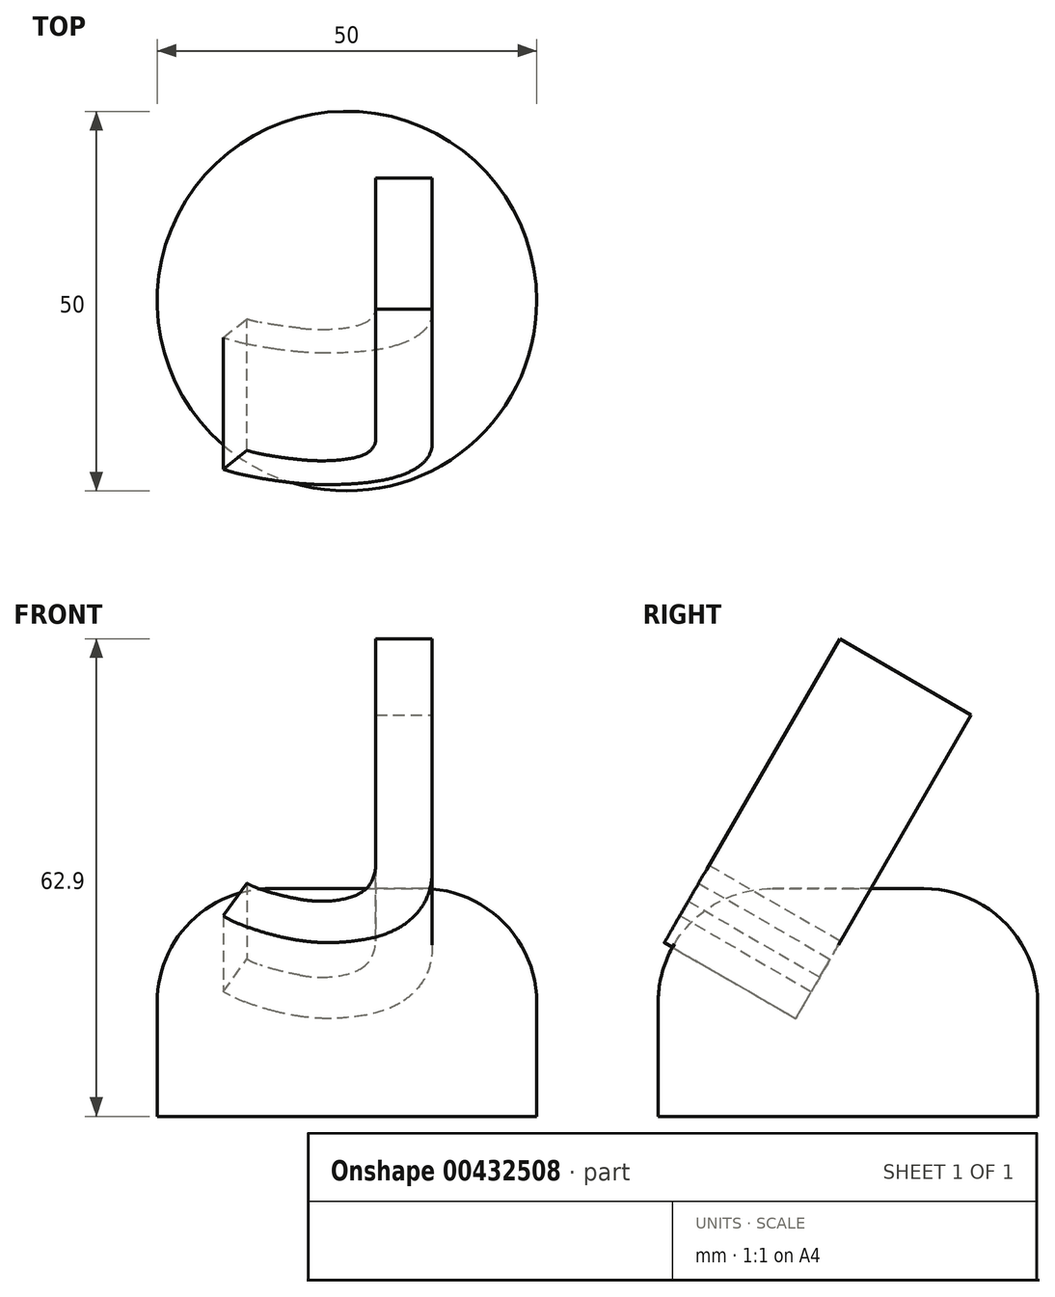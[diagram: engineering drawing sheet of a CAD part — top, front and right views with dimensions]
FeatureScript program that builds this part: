
annotation { "Feature Type Name" : "Feature", "Feature Type Description" : "" }
export const myFeature = defineFeature(function(context is Context, id is Id, definition is map)
    precondition{}
    {
        {
            var Q0;
            Q0=qCreatedBy(makeId("Top.planeOp"),FACE);
            var sketch = newSketch(context, id + "F0", { "sketchPlane" : qUnion([Q0])});
            skText(sketch, "E0", { "text": "J", "fontName": "AllertaStencil-Regular.ttf"});
            const initialGuessF0  = {"E0": [-0.05232, -0.03537, 1, 0, 0.045]};
            skSetInitialGuess(sketch, initialGuessF0);
            skSolve(sketch);
        }
        {
            var Q0;
            Q0=qSketchRegion(id+"F0",true);
            extrude(context, id + "F1", {"entities" : qUnion([Q0]), "depth" : 20 * mm});
        }
        {
            var Q0;
            Q0=makeQuery(id+"F1.opExtrude","SWEPT_BODY",BODY,{"disambiguationData":[OSD([sQuery(id+"F0.wireOp",EDGE,"E0.sketch_text.stroke-0"),sQuery(id+"F0.wireOp",EDGE,"E0.sketch_text.stroke-1"),sQuery(id+"F0.wireOp",EDGE,"E0.sketch_text.stroke-2"),sQuery(id+"F0.wireOp",EDGE,"E0.sketch_text.stroke-3"),sQuery(id+"F0.wireOp",EDGE,"E0.sketch_text.stroke-4"),sQuery(id+"F0.wireOp",EDGE,"E0.sketch_text.stroke-5"),sQuery(id+"F0.wireOp",EDGE,"E0.sketch_text.stroke-6"),sQuery(id+"F0.wireOp",EDGE,"E0.sketch_text.stroke-7"),sQuery(id+"F0.wireOp",EDGE,"E0.sketch_text.stroke-8"),sQuery(id+"F0.wireOp",EDGE,"E0.sketch_text.stroke-9"),sQuery(id+"F0.wireOp",EDGE,"E0.sketch_text.stroke-10"),sQuery(id+"F0.wireOp",EDGE,"E0.sketch_text.stroke-11"),sQuery(id+"F0.wireOp",EDGE,"E0.sketch_text.stroke-12"),sQuery(id+"F0.wireOp",EDGE,"E0.sketch_text.stroke-13")])]});
            transform(context, id + "F2", {"entities" : qUnion([Q0]), "transformType" : TransformType.TRANSLATION_3D, "dx" : 76.45 * mm, "dy" : 0 * mm, "dz" : 0 * mm, "makeCopy" : false});
        }
        {
            var Q0;
            Q0=qCreatedBy(makeId("Top.planeOp"),FACE);
            var sketch = newSketch(context, id + "F3", { "sketchPlane" : qUnion([Q0])});
            skCircle(sketch, "E1", {"center": v(-27.2, 27.91) * mm, "radius": 25 * mm});
            skSolve(sketch);
        }
        {
            var Q0;
            Q0=makeQuery(id+"F1.opExtrude","SWEPT_BODY",BODY,{"disambiguationData":[OSD([sQuery(id+"F0.wireOp",EDGE,"E0.sketch_text.stroke-0"),sQuery(id+"F0.wireOp",EDGE,"E0.sketch_text.stroke-1"),sQuery(id+"F0.wireOp",EDGE,"E0.sketch_text.stroke-2"),sQuery(id+"F0.wireOp",EDGE,"E0.sketch_text.stroke-3"),sQuery(id+"F0.wireOp",EDGE,"E0.sketch_text.stroke-4"),sQuery(id+"F0.wireOp",EDGE,"E0.sketch_text.stroke-5"),sQuery(id+"F0.wireOp",EDGE,"E0.sketch_text.stroke-6"),sQuery(id+"F0.wireOp",EDGE,"E0.sketch_text.stroke-7"),sQuery(id+"F0.wireOp",EDGE,"E0.sketch_text.stroke-8"),sQuery(id+"F0.wireOp",EDGE,"E0.sketch_text.stroke-9"),sQuery(id+"F0.wireOp",EDGE,"E0.sketch_text.stroke-10"),sQuery(id+"F0.wireOp",EDGE,"E0.sketch_text.stroke-11"),sQuery(id+"F0.wireOp",EDGE,"E0.sketch_text.stroke-12"),sQuery(id+"F0.wireOp",EDGE,"E0.sketch_text.stroke-13")])]});
            transform(context, id + "F4", {"entities" : qUnion([Q0]), "transformType" : TransformType.TRANSLATION_3D, "dx" : 27.3 * mm, "dy" : 0 * mm, "dz" : 0 * mm, "makeCopy" : false});
        }
        {
            var Q0;
            Q0=makeQuery(id+"F3.imprint","IMPRINT",FACE,{"disambiguationData":[TD([[makeQuery(id+"F3.imprint","IMPRINT",EDGE,{"derivedFrom":sQuery(id+"F3.wireOp",EDGE,"E1")}),1.0]])]});
            extrude(context, id + "F5", {"entities" : qUnion([Q0]), "depth" : 30 * mm});
        }
        {
            var Q0;
            Q0=makeQuery(id+"F5.opExtrude","CAP_FACE",FACE,{"disambiguationData":[OSD([sQuery(id+"F3.wireOp",EDGE,"E1")])],"isStart":false});
            fillet(context, id + "F6", {"entities" : qUnion([Q0]), "radius" : 15 * mm, "tangentPropagation" : true, "allowEdgeOverflow" : false});
        }
        {
            var Q0;
            Q0=makeQuery(id+"F1.opExtrude","SWEPT_BODY",BODY,{"disambiguationData":[OSD([sQuery(id+"F0.wireOp",EDGE,"E0.sketch_text.stroke-0"),sQuery(id+"F0.wireOp",EDGE,"E0.sketch_text.stroke-1"),sQuery(id+"F0.wireOp",EDGE,"E0.sketch_text.stroke-2"),sQuery(id+"F0.wireOp",EDGE,"E0.sketch_text.stroke-3"),sQuery(id+"F0.wireOp",EDGE,"E0.sketch_text.stroke-4"),sQuery(id+"F0.wireOp",EDGE,"E0.sketch_text.stroke-5"),sQuery(id+"F0.wireOp",EDGE,"E0.sketch_text.stroke-6"),sQuery(id+"F0.wireOp",EDGE,"E0.sketch_text.stroke-7"),sQuery(id+"F0.wireOp",EDGE,"E0.sketch_text.stroke-8"),sQuery(id+"F0.wireOp",EDGE,"E0.sketch_text.stroke-9"),sQuery(id+"F0.wireOp",EDGE,"E0.sketch_text.stroke-10"),sQuery(id+"F0.wireOp",EDGE,"E0.sketch_text.stroke-11"),sQuery(id+"F0.wireOp",EDGE,"E0.sketch_text.stroke-12"),sQuery(id+"F0.wireOp",EDGE,"E0.sketch_text.stroke-13")])]});
            var Q1;
            Q1=makeQuery(id+"F1.opExtrude","CAP_EDGE",EDGE,{"disambiguationData":[OSD([sQuery(id+"F0.wireOp",EDGE,"E0.sketch_text.stroke-17")])],"isStart":false});
            transform(context, id + "F7", {"entities" : qUnion([Q0]), "transformType" : TransformType.ROTATION, "transformAxis" : qUnion([Q1]), "angle" : 60 * degree, "makeCopy" : false});
        }
        {
            var Q0;
            Q0=makeQuery(id+"F1.opExtrude","SWEPT_BODY",BODY,{"disambiguationData":[OSD([sQuery(id+"F0.wireOp",EDGE,"E0.sketch_text.stroke-0"),sQuery(id+"F0.wireOp",EDGE,"E0.sketch_text.stroke-1"),sQuery(id+"F0.wireOp",EDGE,"E0.sketch_text.stroke-2"),sQuery(id+"F0.wireOp",EDGE,"E0.sketch_text.stroke-3"),sQuery(id+"F0.wireOp",EDGE,"E0.sketch_text.stroke-4"),sQuery(id+"F0.wireOp",EDGE,"E0.sketch_text.stroke-5"),sQuery(id+"F0.wireOp",EDGE,"E0.sketch_text.stroke-6"),sQuery(id+"F0.wireOp",EDGE,"E0.sketch_text.stroke-7"),sQuery(id+"F0.wireOp",EDGE,"E0.sketch_text.stroke-8"),sQuery(id+"F0.wireOp",EDGE,"E0.sketch_text.stroke-9"),sQuery(id+"F0.wireOp",EDGE,"E0.sketch_text.stroke-10"),sQuery(id+"F0.wireOp",EDGE,"E0.sketch_text.stroke-11"),sQuery(id+"F0.wireOp",EDGE,"E0.sketch_text.stroke-12"),sQuery(id+"F0.wireOp",EDGE,"E0.sketch_text.stroke-13")])]});
            transform(context, id + "F8", {"entities" : qUnion([Q0]), "transformType" : TransformType.TRANSLATION_3D, "dx" : -96.5 * mm, "dy" : 16.3 * mm, "dz" : 42.9 * mm, "makeCopy" : false});
        }
    });
